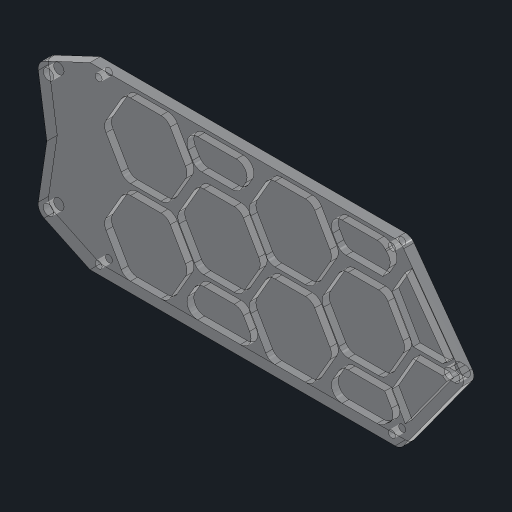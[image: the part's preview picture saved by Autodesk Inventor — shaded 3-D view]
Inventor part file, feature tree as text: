
AUTODESK INVENTOR PART (.ipt)
format: ipt  version: 2023.2 (Build 272271030, 271C)  size: 559,616 bytes
history: native  units: mm
features: extrude x3, fillet x2, sketch x2, projected_geometry x2
ambient origin geometry x8: Origin, YZ Plane, XZ Plane, XY Plane, X Axis, Y Axis, Z Axis, Center Point
bodies: Solid1 (feature_tree)
feature tree (9):
  extrude  "Extrusion1"  Depth=42.0mm
  extrude  "Extrusion2"  Depth=2.5mm
  fillet  "Fillet2"  Radius=36.0mm
  extrude  "Extrusion5"  Depth=2.5mm
  fillet  "Fillet3"  Radius=8.0mm
  sketch  "Sketch1"  dims[d0=90.0mm d1=42.0mm]
  projected_geometry  "Projected Loop1"
  sketch  "Sketch5"  dims[d2=5.0mm d3=22.0mm d5=36.0mm d6=127.0mm d7=8.0mm d8=8.0mm d9=4.0mm d10=3.0mm d11=3.0mm d12=8.0mm d13=3.0mm d14=1.5mm d15=8.5mm d16=1.25mm d17=5.0mm d18=5.0mm d19=1.0mm d20=3.0mm d21=16.0mm d22=12.0mm d23=1.0mm d24=1.0mm d25=1.0mm d26=2.0mm d27=1.0mm d28=2.0mm d29=2.0mm d30=2.0mm d31=2.0mm d32=2.0mm d33=1.0mm d34=5.0mm d35=5.0mm d36=5.0mm d37=1.5mm d38=1.5mm d39=3.0mm d40=0.0mm d42=5.0mm d43=1.6mm d44=0.0mm d52=3.1mm d71=3.0mm d74=3.0mm d75=2.5mm d76=3.0mm d77=3.0mm d78=21.5mm d83=3.0mm d84=3.0mm d85=3.0mm d86=3.0mm d87=3.0mm d88=3.0mm d89=3.0mm d90=41.857895mm d91=30.0mm d93=41.857895mm d94=10.0mm d96=10.0mm d98=2.0mm d99=0.0mm d100=3.1mm d101=1.5mm d102=2.0mm d103=2.5mm d104=2.5mm d105=2.5mm d106=2.5mm]
  projected_geometry  "Projected Loop5"
